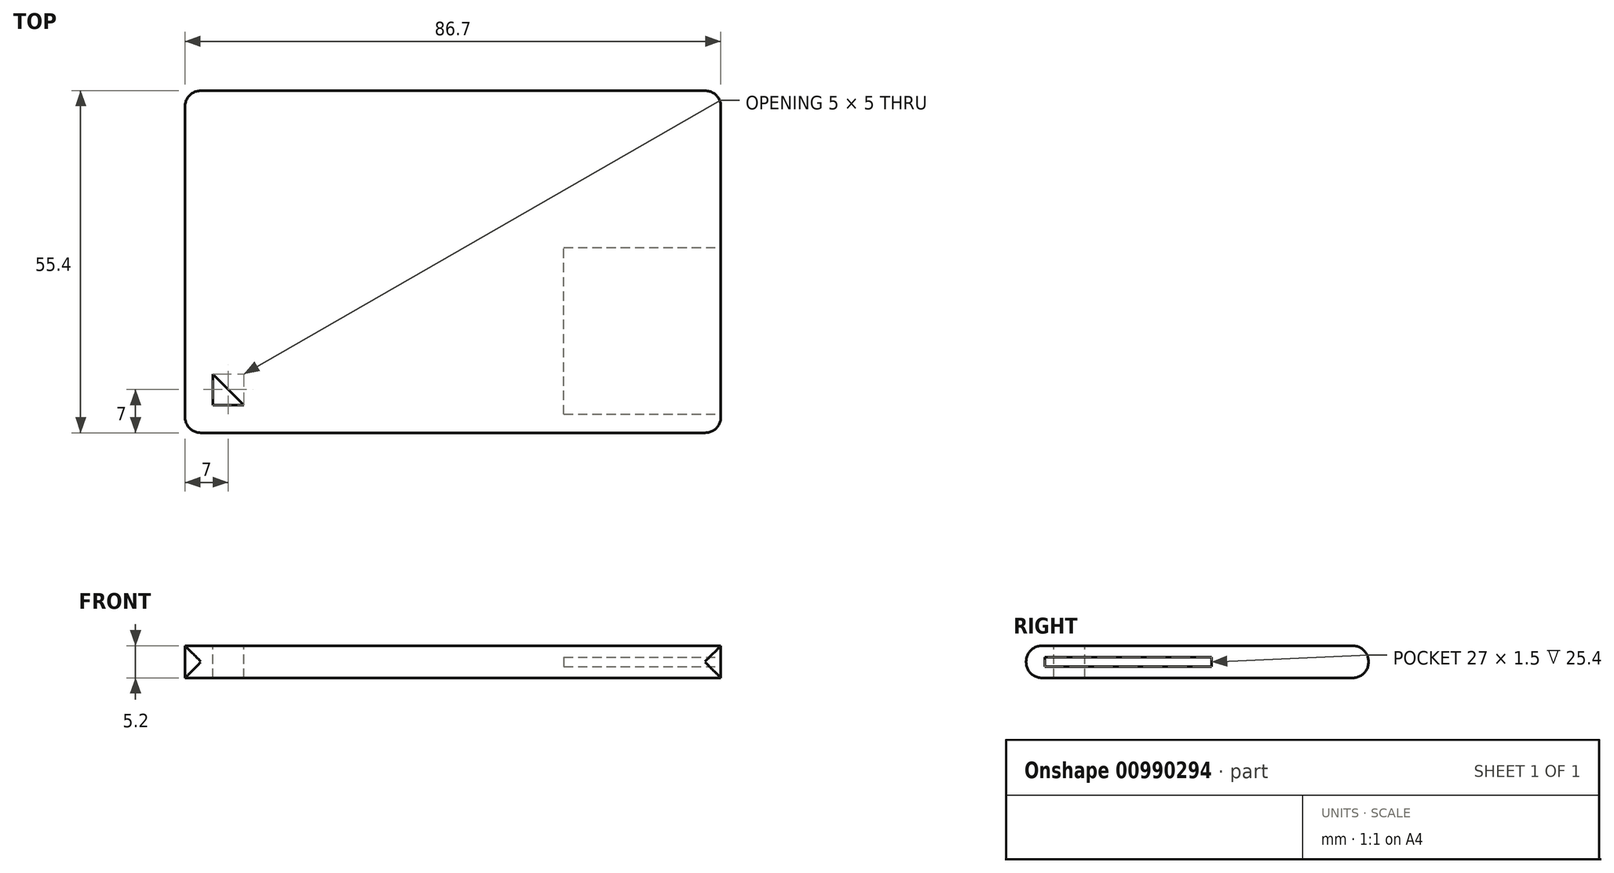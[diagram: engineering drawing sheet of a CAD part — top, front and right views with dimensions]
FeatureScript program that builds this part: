
annotation { "Feature Type Name" : "Feature", "Feature Type Description" : "" }
export const myFeature = defineFeature(function(context is Context, id is Id, definition is map)
    precondition{}
    {
        {
            var Q0;
            Q0=qCreatedBy(makeId("Top.planeOp"),FACE);
            var sketch = newSketch(context, id + "F0", { "sketchPlane" : qUnion([Q0])});
            skLineSegment(sketch, "E0.bottom", {"start": v(0, 0) * mm, "end": v(86.7, 0) * mm});
            skLineSegment(sketch, "E0.top", {"start": v(0, 55.4) * mm, "end": v(86.7, 55.4) * mm});
            skLineSegment(sketch, "E0.left", {"start": v(0, 0) * mm, "end": v(0, 55.4) * mm});
            skLineSegment(sketch, "E0.right", {"start": v(86.7, 0) * mm, "end": v(86.7, 55.4) * mm});
            skSolve(sketch);
        }
        {
            var Q0;
            Q0 = qSketchRegion(id + "F0", true);
            extrude(context, id + "F1", {"entities" : qUnion([Q0]), "depth" : 5.2 * mm, "offsetDistance" : 25.4 * mm});
        }
        {
            var Q0;
            Q0=makeQuery(id+"F1.opExtrude","CAP_EDGE",EDGE,{"disambiguationData":[OSD([sQuery(id+"F0.wireOp",EDGE,"E0.bottom")])],"isStart":false});
            var Q1;
            Q1=makeQuery(id+"F1.opExtrude","CAP_EDGE",EDGE,{"disambiguationData":[OSD([sQuery(id+"F0.wireOp",EDGE,"E0.bottom")])],"isStart":true});
            var Q2;
            Q2=makeQuery(id+"F1.opExtrude","CAP_EDGE",EDGE,{"disambiguationData":[OSD([sQuery(id+"F0.wireOp",EDGE,"E0.top")])],"isStart":false});
            var Q3;
            Q3=makeQuery(id+"F1.opExtrude","CAP_EDGE",EDGE,{"disambiguationData":[OSD([sQuery(id+"F0.wireOp",EDGE,"E0.top")])],"isStart":true});
            var Q4;
            Q4=makeQuery(id+"F1.opExtrude","SWEPT_EDGE",EDGE,{"disambiguationData":[OSD([sQuery(id+"F0.wireOp",EDGE,"E0.bottom"),sQuery(id+"F0.wireOp",EDGE,"E0.right")])]});
            var Q5;
            Q5=makeQuery(id+"F1.opExtrude","SWEPT_EDGE",EDGE,{"disambiguationData":[OSD([sQuery(id+"F0.wireOp",EDGE,"E0.bottom"),sQuery(id+"F0.wireOp",EDGE,"E0.left")])]});
            var Q6;
            Q6=makeQuery(id+"F1.opExtrude","SWEPT_EDGE",EDGE,{"disambiguationData":[OSD([sQuery(id+"F0.wireOp",EDGE,"E0.top"),sQuery(id+"F0.wireOp",EDGE,"E0.left")])]});
            var Q7;
            Q7=makeQuery(id+"F1.opExtrude","SWEPT_EDGE",EDGE,{"disambiguationData":[OSD([sQuery(id+"F0.wireOp",EDGE,"E0.top"),sQuery(id+"F0.wireOp",EDGE,"E0.right")])]});
            fillet(context, id + "F2", {"entities" : qUnion([Q0, Q1, Q2, Q3, Q4, Q5, Q6, Q7]), "radius" : 2.54 * mm, "tangentPropagation" : true, "allowEdgeOverflow" : false});
        }
        {
            var Q0;
            Q0=makeQuery(id+"F1.opExtrude","CAP_FACE",FACE,{"disambiguationData":[OSD([sQuery(id+"F0.wireOp",EDGE,"E0.bottom"),sQuery(id+"F0.wireOp",EDGE,"E0.top"),sQuery(id+"F0.wireOp",EDGE,"E0.left"),sQuery(id+"F0.wireOp",EDGE,"E0.right")])],"isStart":false});
            var sketch = newSketch(context, id + "F3", { "sketchPlane" : qUnion([Q0])});
            skLineSegment(sketch, "E1", {"start": v(4.5, 9.5) * mm, "end": v(4.5, 4.5) * mm});
            skLineSegment(sketch, "E2", {"start": v(4.5, 4.5) * mm, "end": v(9.5, 4.5) * mm});
            skLineSegment(sketch, "E3", {"start": v(9.5, 4.5) * mm, "end": v(4.5, 9.5) * mm});
            skSolve(sketch);
        }
        {
            var Q0;
            Q0 = qSketchRegion(id + "F3", true);
            extrude(context, id + "F4", {"entities" : qUnion([Q0]), "operationType" : NewBodyOperationType.REMOVE, "oppositeDirection" : true, "depth" : 25.4 * mm, "offsetDistance" : 25.4 * mm});
        }
        {
            var Q0;
            Q0=makeQuery(id+"F1.opExtrude","CAP_FACE",FACE,{"disambiguationData":[OSD([sQuery(id+"F0.wireOp",EDGE,"E0.bottom"),sQuery(id+"F0.wireOp",EDGE,"E0.top"),sQuery(id+"F0.wireOp",EDGE,"E0.left"),sQuery(id+"F0.wireOp",EDGE,"E0.right")])],"isStart":false});
            var sketch = newSketch(context, id + "F5", { "sketchPlane" : qUnion([Q0])});
            skLineSegment(sketch, "E4.bottom", {"start": v(6.3, 11.6) * mm, "end": v(40, 11.6) * mm, "construction": true});
            skLineSegment(sketch, "E4.top", {"start": v(6.3, 24.6) * mm, "end": v(40, 24.6) * mm, "construction": true});
            skLineSegment(sketch, "E4.left", {"start": v(6.3, 11.6) * mm, "end": v(6.3, 24.6) * mm, "construction": true});
            skLineSegment(sketch, "E4.right", {"start": v(40, 11.6) * mm, "end": v(40, 24.6) * mm, "construction": true});
            skSolve(sketch);
        }
        {
            var Q0;
            Q0=makeQuery(id+"F1.opExtrude","SWEPT_FACE",FACE,{"disambiguationData":[OSD([sQuery(id+"F0.wireOp",EDGE,"E0.right")])]});
            var sketch = newSketch(context, id + "F6", { "sketchPlane" : qUnion([Q0])});
            skLineSegment(sketch, "E5.bottom", {"start": v(3, 3.35) * mm, "end": v(30, 3.35) * mm});
            skLineSegment(sketch, "E5.top", {"start": v(3, 1.85) * mm, "end": v(30, 1.85) * mm});
            skLineSegment(sketch, "E5.left", {"start": v(3, 3.35) * mm, "end": v(3, 1.85) * mm});
            skLineSegment(sketch, "E5.right", {"start": v(30, 3.35) * mm, "end": v(30, 1.85) * mm});
            skLineSegment(sketch, "E6", {"start": v(52.86, 2.6) * mm, "end": v(2.54, 2.6) * mm, "construction": true});
            skPoint(sketch, "E7", {"position": v(30, 2.6) * mm});
            skSolve(sketch);
        }
        {
            var Q0;
            Q0 = qSketchRegion(id + "F6", true);
            extrude(context, id + "F7", {"entities" : qUnion([Q0]), "operationType" : NewBodyOperationType.REMOVE, "oppositeDirection" : true, "depth" : 25.4 * mm, "offsetDistance" : 25.4 * mm});
        }
    });
